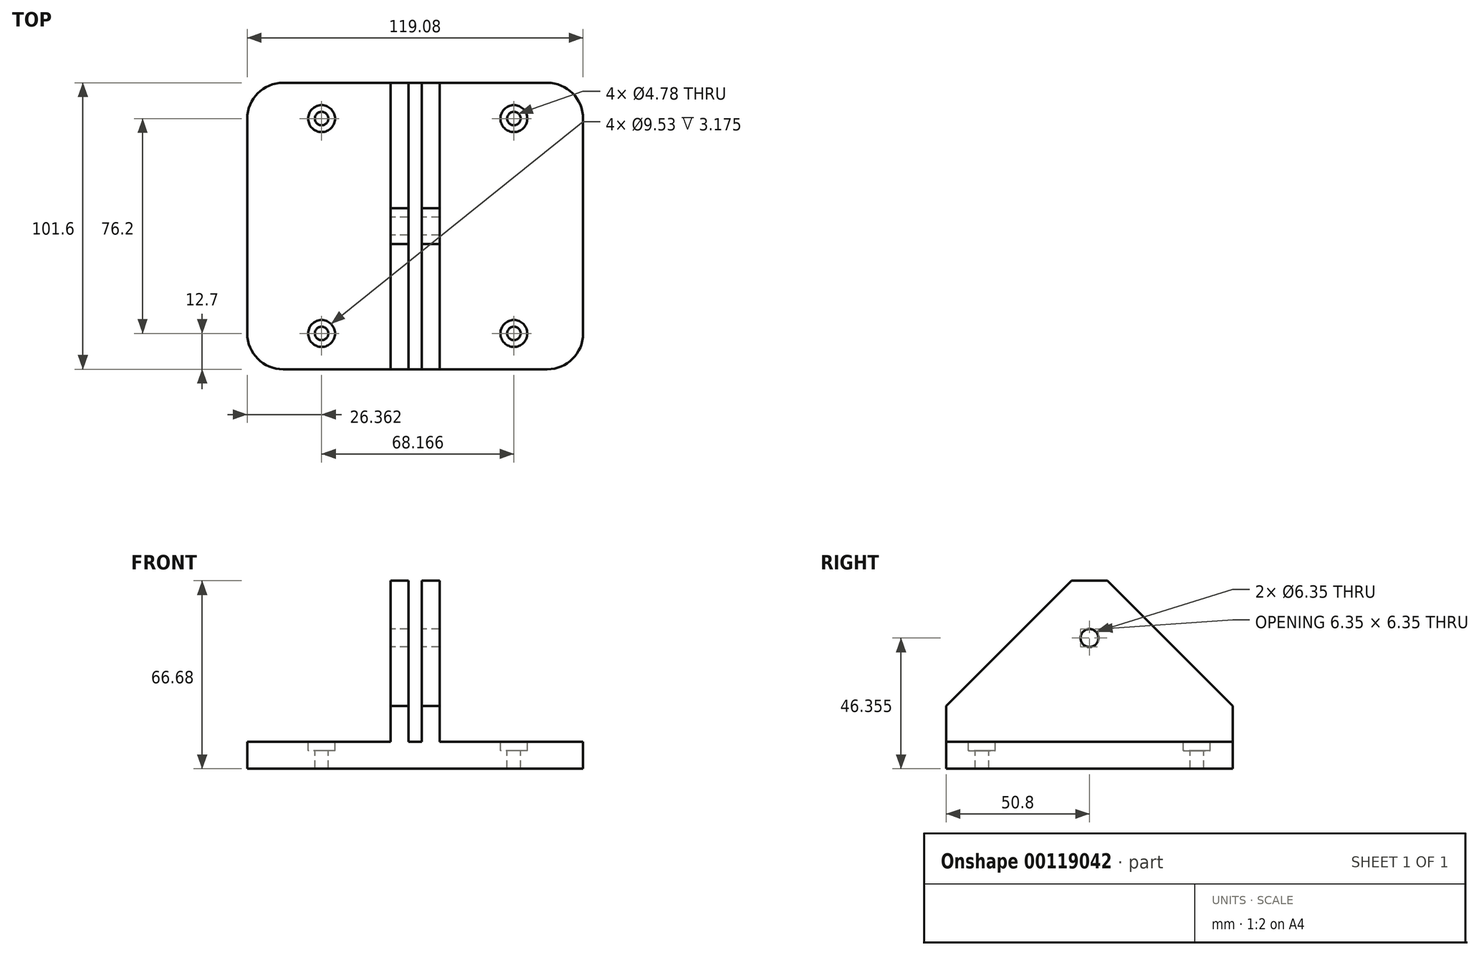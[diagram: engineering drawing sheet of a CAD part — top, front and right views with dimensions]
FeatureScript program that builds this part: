
annotation { "Feature Type Name" : "Feature", "Feature Type Description" : "" }
export const myFeature = defineFeature(function(context is Context, id is Id, definition is map)
    precondition{}
    {
        {
            var Q0;
            Q0=qCreatedBy(makeId("Front.planeOp"),FACE);
            var sketch = newSketch(context, id + "F0", { "sketchPlane" : qUnion([Q0])});
            skLineSegment(sketch, "E0", {"start": v(0, 0) * mm, "end": v(0, 9.53) * mm});
            skLineSegment(sketch, "E1", {"start": v(0, 9.53) * mm, "end": v(50.8, 9.53) * mm});
            skLineSegment(sketch, "E2", {"start": v(50.8, 9.52) * mm, "end": v(50.8, 66.68) * mm});
            skLineSegment(sketch, "E3", {"start": v(50.8, 66.68) * mm, "end": v(57.15, 66.68) * mm});
            skLineSegment(sketch, "E4", {"start": v(57.15, 66.68) * mm, "end": v(57.15, 9.53) * mm});
            skLineSegment(sketch, "E5", {"start": v(57.15, 9.53) * mm, "end": v(61.93, 9.53) * mm});
            skLineSegment(sketch, "E6", {"start": v(61.93, 9.53) * mm, "end": v(61.93, 66.68) * mm});
            skLineSegment(sketch, "E7", {"start": v(61.93, 66.68) * mm, "end": v(68.28, 66.68) * mm});
            skLineSegment(sketch, "E8", {"start": v(68.28, 66.68) * mm, "end": v(68.28, 9.53) * mm});
            skLineSegment(sketch, "E9", {"start": v(68.28, 9.53) * mm, "end": v(119.08, 9.53) * mm});
            skLineSegment(sketch, "E10", {"start": v(119.08, 9.53) * mm, "end": v(119.08, 0) * mm});
            skLineSegment(sketch, "E11", {"start": v(119.08, 0) * mm, "end": v(0, 0) * mm});
            skSolve(sketch);
        }
        {
            var Q0;
            Q0 = qSketchRegion(id + "F0", true);
            extrude(context, id + "F1", {"entities" : qUnion([Q0]), "depth" : 101.6 * mm});
        }
        {
            var Q0;
            Q0=makeQuery(id+"F1.opExtrude","SWEPT_FACE",FACE,{"disambiguationData":[OSD([sQuery(id+"F0.wireOp",EDGE,"E1")])]});
            var sketch = newSketch(context, id + "F2", { "sketchPlane" : qUnion([Q0])});
            skPoint(sketch, "E12", {"position": v(26.36, -88.9) * mm});
            skPoint(sketch, "E13", {"position": v(26.36, -12.7) * mm});
            skSolve(sketch);
        }
        {
            var Q0;
            Q0=sQuery(id+"F2.wireOp",VERTEX,"E13");
            var Q1;
            Q1=sQuery(id+"F2.wireOp",VERTEX,"E12");
            var Q2;
            Q2=makeQuery(id+"F1.opExtrude","SWEPT_BODY",BODY,{"disambiguationData":[OSD([sQuery(id+"F0.wireOp",EDGE,"E0"),sQuery(id+"F0.wireOp",EDGE,"E1"),sQuery(id+"F0.wireOp",EDGE,"E2"),sQuery(id+"F0.wireOp",EDGE,"E3"),sQuery(id+"F0.wireOp",EDGE,"E4"),sQuery(id+"F0.wireOp",EDGE,"E5"),sQuery(id+"F0.wireOp",EDGE,"E6"),sQuery(id+"F0.wireOp",EDGE,"E7"),sQuery(id+"F0.wireOp",EDGE,"E8"),sQuery(id+"F0.wireOp",EDGE,"E9"),sQuery(id+"F0.wireOp",EDGE,"E10"),sQuery(id+"F0.wireOp",EDGE,"E11")])]});
            hole(context, id + "F3", {"style" : HoleStyle.C_BORE, "endStyle" : HoleEndStyle.THROUGH, "holeDiameter" : 4.78 * mm, "cBoreDiameter" : 9.52 * mm, "cBoreDepth" : 3.17 * mm, "locations" : qUnion([Q0, Q1]), "scope" : qUnion([Q2]), "isTappedThrough" : true});
        }
        {
            var Q0;
            Q0=makeQuery(id+"F1.opExtrude","SWEPT_FACE",FACE,{"disambiguationData":[OSD([sQuery(id+"F0.wireOp",EDGE,"E9")])]});
            var sketch = newSketch(context, id + "F4", { "sketchPlane" : qUnion([Q0])});
            skPoint(sketch, "E14", {"position": v(94.53, -12.7) * mm});
            skPoint(sketch, "E15", {"position": v(94.53, -88.9) * mm});
            skSolve(sketch);
        }
        {
            var Q0;
            Q0=sQuery(id+"F4.wireOp",VERTEX,"E14");
            var Q1;
            Q1=sQuery(id+"F4.wireOp",VERTEX,"E15");
            var Q2;
            Q2=makeQuery(id+"F1.opExtrude","SWEPT_BODY",BODY,{"disambiguationData":[OSD([sQuery(id+"F0.wireOp",EDGE,"E0"),sQuery(id+"F0.wireOp",EDGE,"E1"),sQuery(id+"F0.wireOp",EDGE,"E2"),sQuery(id+"F0.wireOp",EDGE,"E3"),sQuery(id+"F0.wireOp",EDGE,"E4"),sQuery(id+"F0.wireOp",EDGE,"E5"),sQuery(id+"F0.wireOp",EDGE,"E6"),sQuery(id+"F0.wireOp",EDGE,"E7"),sQuery(id+"F0.wireOp",EDGE,"E8"),sQuery(id+"F0.wireOp",EDGE,"E9"),sQuery(id+"F0.wireOp",EDGE,"E10"),sQuery(id+"F0.wireOp",EDGE,"E11")])]});
            hole(context, id + "F5", {"style" : HoleStyle.C_BORE, "endStyle" : HoleEndStyle.THROUGH, "holeDiameter" : 4.78 * mm, "cBoreDiameter" : 9.52 * mm, "cBoreDepth" : 3.17 * mm, "locations" : qUnion([Q0, Q1]), "scope" : qUnion([Q2]), "isTappedThrough" : true});
        }
        {
            var Q0;
            Q0=makeQuery(id+"F1.opExtrude","SWEPT_FACE",FACE,{"disambiguationData":[OSD([sQuery(id+"F0.wireOp",EDGE,"E2")])]});
            var sketch = newSketch(context, id + "F6", { "sketchPlane" : qUnion([Q0])});
            skPoint(sketch, "E16", {"position": v(50.8, 46.35) * mm});
            skSolve(sketch);
        }
        {
            var Q0;
            Q0=sQuery(id+"F6.wireOp",VERTEX,"E16");
            var Q1;
            Q1=makeQuery(id+"F1.opExtrude","SWEPT_BODY",BODY,{"disambiguationData":[OSD([sQuery(id+"F0.wireOp",EDGE,"E0"),sQuery(id+"F0.wireOp",EDGE,"E1"),sQuery(id+"F0.wireOp",EDGE,"E2"),sQuery(id+"F0.wireOp",EDGE,"E3"),sQuery(id+"F0.wireOp",EDGE,"E4"),sQuery(id+"F0.wireOp",EDGE,"E5"),sQuery(id+"F0.wireOp",EDGE,"E6"),sQuery(id+"F0.wireOp",EDGE,"E7"),sQuery(id+"F0.wireOp",EDGE,"E8"),sQuery(id+"F0.wireOp",EDGE,"E9"),sQuery(id+"F0.wireOp",EDGE,"E10"),sQuery(id+"F0.wireOp",EDGE,"E11")])]});
            hole(context, id + "F7", {"style" : HoleStyle.SIMPLE, "endStyle" : HoleEndStyle.THROUGH, "holeDiameter" : 6.35 * mm, "locations" : qUnion([Q0]), "scope" : qUnion([Q1]), "isTappedThrough" : true});
        }
        {
            var Q0;
            Q0=makeQuery(id+"F1.opExtrude","CAP_EDGE",EDGE,{"disambiguationData":[OSD([sQuery(id+"F0.wireOp",EDGE,"E3")])],"isStart":true});
            var Q1;
            Q1=makeQuery(id+"F1.opExtrude","CAP_EDGE",EDGE,{"disambiguationData":[OSD([sQuery(id+"F0.wireOp",EDGE,"E3")])],"isStart":false});
            var Q2;
            Q2=makeQuery(id+"F1.opExtrude","CAP_EDGE",EDGE,{"disambiguationData":[OSD([sQuery(id+"F0.wireOp",EDGE,"E7")])],"isStart":true});
            var Q3;
            Q3=makeQuery(id+"F1.opExtrude","CAP_EDGE",EDGE,{"disambiguationData":[OSD([sQuery(id+"F0.wireOp",EDGE,"E7")])],"isStart":false});
            chamfer(context, id + "F8", {"entities" : qUnion([Q0, Q1, Q2, Q3]), "width" : 44.45 * mm, "tangentPropagation" : true});
        }
        {
            var Q0;
            Q0=makeQuery(id+"F1.opExtrude","CAP_EDGE",EDGE,{"disambiguationData":[OSD([sQuery(id+"F0.wireOp",EDGE,"E0")])],"isStart":true});
            var Q1;
            Q1=makeQuery(id+"F1.opExtrude","CAP_EDGE",EDGE,{"disambiguationData":[OSD([sQuery(id+"F0.wireOp",EDGE,"E0")])],"isStart":false});
            var Q2;
            Q2=makeQuery(id+"F1.opExtrude","CAP_EDGE",EDGE,{"disambiguationData":[OSD([sQuery(id+"F0.wireOp",EDGE,"E10")])],"isStart":false});
            var Q3;
            Q3=makeQuery(id+"F1.opExtrude","CAP_EDGE",EDGE,{"disambiguationData":[OSD([sQuery(id+"F0.wireOp",EDGE,"E10")])],"isStart":true});
            fillet(context, id + "F9", {"entities" : qUnion([Q0, Q1, Q2, Q3]), "radius" : 12.7 * mm, "tangentPropagation" : true, "allowEdgeOverflow" : false});
        }
    });
